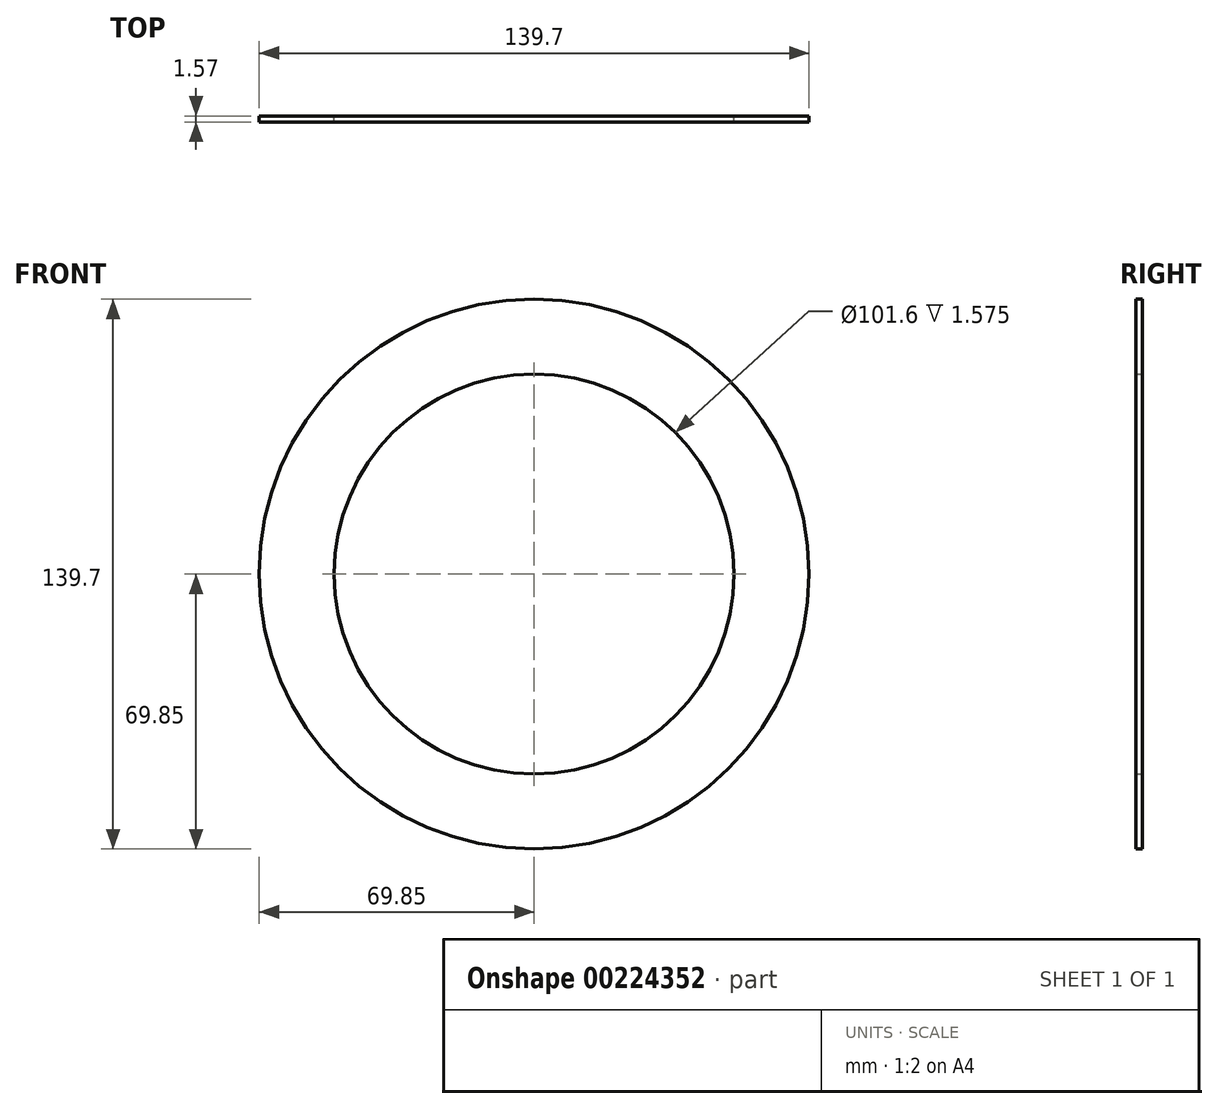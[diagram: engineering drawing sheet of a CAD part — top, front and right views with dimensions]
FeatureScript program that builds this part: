
annotation { "Feature Type Name" : "Feature", "Feature Type Description" : "" }
export const myFeature = defineFeature(function(context is Context, id is Id, definition is map)
    precondition{}
    {
        {
            var Q0;
            Q0=qCreatedBy(makeId("Front.planeOp"),FACE);
            var sketch = newSketch(context, id + "F0", { "sketchPlane" : qUnion([Q0])});
            skCircle(sketch, "E0", {"center": v(0, 0) * mm, "radius": 69.85 * mm});
            skCircle(sketch, "E1", {"center": v(0, 0) * mm, "radius": 50.8 * mm});
            skSolve(sketch);
        }
        {
            var Q0;
            Q0=makeQuery(id+"F0.imprint","IMPRINT",FACE,{"disambiguationData":[TD([[makeQuery(id+"F0.imprint","IMPRINT",EDGE,{"derivedFrom":sQuery(id+"F0.wireOp",EDGE,"E0")}),1.0]])]});
            extrude(context, id + "F1", {"entities" : qUnion([Q0]), "depth" : 1.57 * mm});
        }
    });
